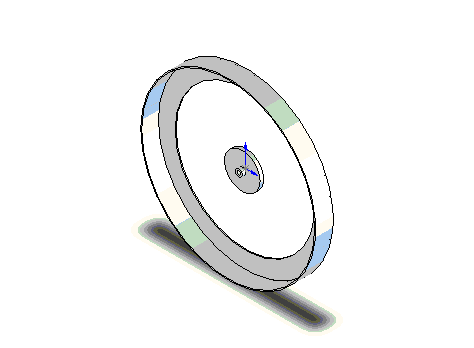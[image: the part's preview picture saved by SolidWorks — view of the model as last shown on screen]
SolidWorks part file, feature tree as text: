
SOLIDWORKS PART (.sldprt)
format: sldprt  version: not decoded by parser v0  size: 125,440 bytes
history: native  units: mm
features: sketch x4, extrude x4 (+11 scaffold rows collapsed)
feature tree (19):
  scaffold x11  (default folders/planes/origin — collapsed)
  sketch  "Sketch1"  dims[c1.D1=250.0mm c1.D2=174.56mm c1.D3=87.28mm c2.D2=87.28mm]
  extrude  "Extrude1"  Depth=1.42mm
  sketch  "Sketch4"  dims[D1=~121.907184mm]
  extrude  "Extrude2"  Depth=23.8mm
  sketch  "Sketch5"  dims[D1=~5.723813mm]
  extrude  "Extrude3"  Depth=5mm
  sketch  "Sketch6"  dims[D1=7.9375mm]
  extrude  "Extrude4"  Depth=5mm
decode coverage: 8 of 8 modeling features carry decoded parameters
note: ~ marks probable driven/reference dimensions
note: suppression state not decoded; provenance and decode notes live in map.json
